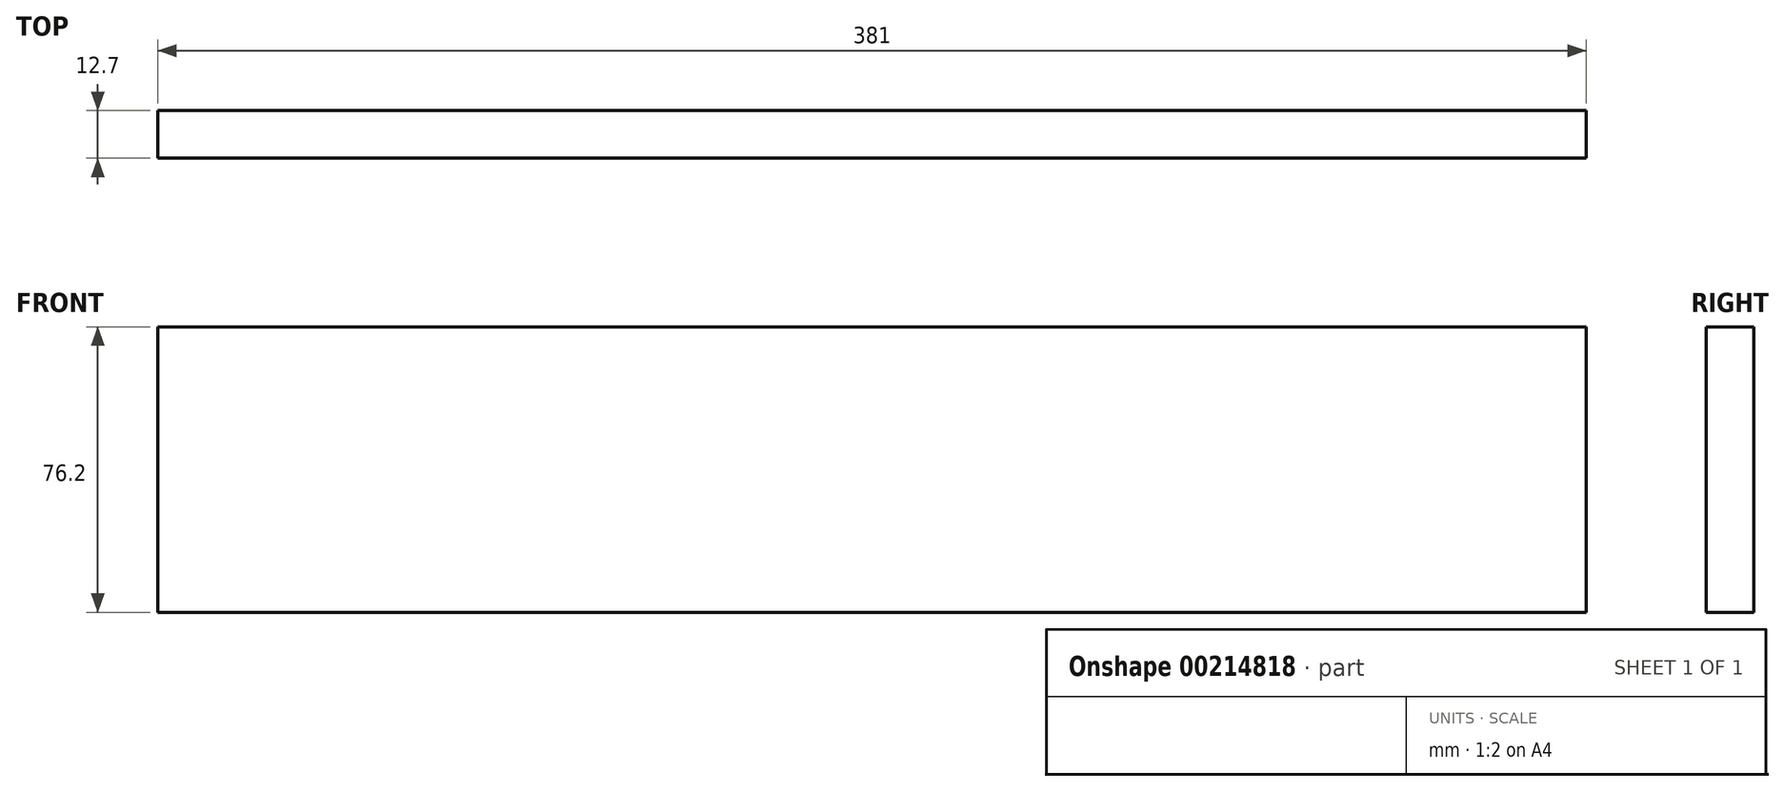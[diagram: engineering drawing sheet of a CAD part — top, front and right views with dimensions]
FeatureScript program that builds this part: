
annotation { "Feature Type Name" : "Feature", "Feature Type Description" : "" }
export const myFeature = defineFeature(function(context is Context, id is Id, definition is map)
    precondition{}
    {
        {
            var Q0;
            Q0=qCreatedBy(makeId("Front.planeOp"),FACE);
            var sketch = newSketch(context, id + "F0", { "sketchPlane" : qUnion([Q0])});
            skLineSegment(sketch, "E0.bottom", {"start": v(0, 0) * mm, "end": v(381, 0) * mm});
            skLineSegment(sketch, "E0.top", {"start": v(0, -76.2) * mm, "end": v(381, -76.2) * mm});
            skLineSegment(sketch, "E0.left", {"start": v(0, 0) * mm, "end": v(0, -76.2) * mm});
            skLineSegment(sketch, "E0.right", {"start": v(381, 0) * mm, "end": v(381, -76.2) * mm});
            skSolve(sketch);
        }
        {
            var Q0;
            Q0=makeQuery(id+"F0.imprint","IMPRINT",FACE,{"disambiguationData":[TD([[makeQuery(id+"F0.imprint","IMPRINT",EDGE,{"derivedFrom":sQuery(id+"F0.wireOp",EDGE,"E0.bottom")}),-1.0]])]});
            extrude(context, id + "F1", {"entities" : qUnion([Q0]), "depth" : 12.7 * mm});
        }
    });
